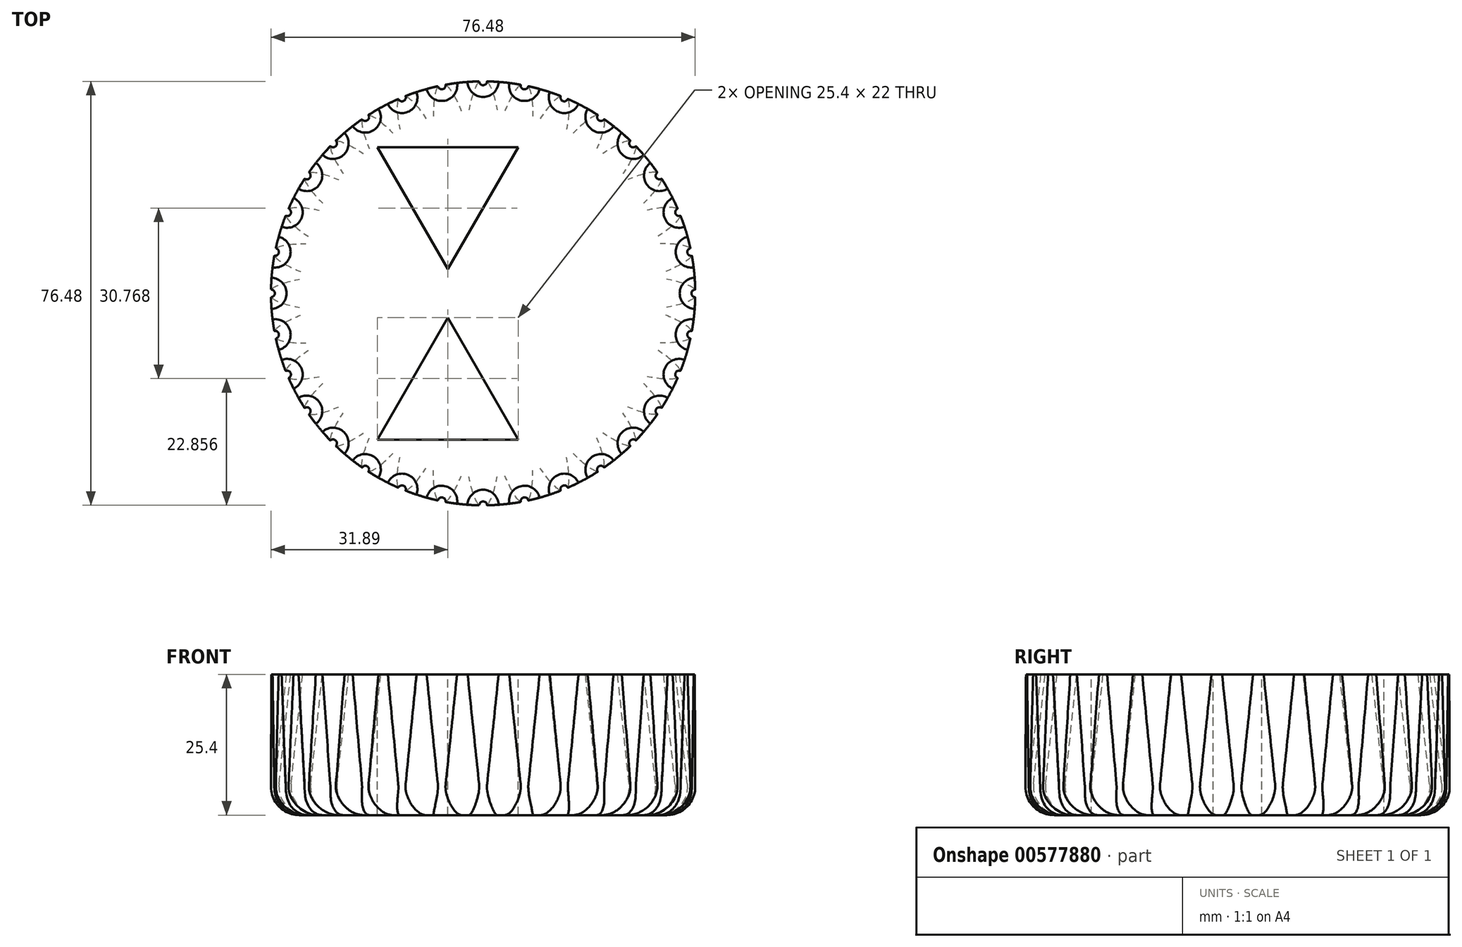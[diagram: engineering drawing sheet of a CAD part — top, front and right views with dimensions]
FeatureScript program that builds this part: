
annotation { "Feature Type Name" : "Feature", "Feature Type Description" : "" }
export const myFeature = defineFeature(function(context is Context, id is Id, definition is map)
    precondition{}
    {
        {
            var Q0;
            Q0=qCreatedBy(makeId("Top.planeOp"),FACE);
            var sketch = newSketch(context, id + "F0", { "sketchPlane" : qUnion([Q0])});
            skCircle(sketch, "E0", {"center": v(0, 0) * mm, "radius": 38.25 * mm});
            skSolve(sketch);
        }
        {
            var Q0;
            Q0=makeQuery(id+"F0.imprint","IMPRINT",FACE,{"disambiguationData":[TD([[makeQuery(id+"F0.imprint","IMPRINT",EDGE,{"derivedFrom":sQuery(id+"F0.wireOp",EDGE,"E0")}),1.0]])]});
            var Q1;
            Q1=sQuery(id+"F0.wireOp",EDGE,"E0");
            extrude(context, id + "F1", {"entities" : qUnion([Q0]), "surfaceEntities" : qUnion([Q1]), "depth" : 25.4 * mm, "offsetDistance" : 25.4 * mm});
        }
        {
            var Q0;
            Q0=makeQuery(id+"F1.opExtrude","CAP_FACE",FACE,{"disambiguationData":[OSD([sQuery(id+"F0.wireOp",EDGE,"E0")])],"isStart":false});
            var sketch = newSketch(context, id + "F2", { "sketchPlane" : qUnion([Q0])});
            skCircle(sketch, "E1", {"center": v(0, 38.25) * mm, "radius": 2.8 * mm});
            skCircle(sketch, "E2.1.0", {"center": v(-7.46, 37.51) * mm, "radius": 2.8 * mm});
            skCircle(sketch, "E2.2.0", {"center": v(-14.64, 35.33) * mm, "radius": 2.8 * mm});
            skCircle(sketch, "E2.3.0", {"center": v(-21.25, 31.8) * mm, "radius": 2.8 * mm});
            skCircle(sketch, "E2.4.0", {"center": v(-27.04, 27.04) * mm, "radius": 2.8 * mm});
            skCircle(sketch, "E2.5.0", {"center": v(-31.8, 21.25) * mm, "radius": 2.8 * mm});
            skCircle(sketch, "E2.6.0", {"center": v(-35.33, 14.64) * mm, "radius": 2.8 * mm});
            skCircle(sketch, "E2.7.0", {"center": v(-37.51, 7.46) * mm, "radius": 2.8 * mm});
            skCircle(sketch, "E2.8.0", {"center": v(-38.25, 0) * mm, "radius": 2.8 * mm});
            skCircle(sketch, "E2.9.0", {"center": v(-37.51, -7.46) * mm, "radius": 2.8 * mm});
            skCircle(sketch, "E2.10.0", {"center": v(-35.33, -14.64) * mm, "radius": 2.8 * mm});
            skCircle(sketch, "E2.11.0", {"center": v(-31.8, -21.25) * mm, "radius": 2.8 * mm});
            skCircle(sketch, "E2.12.0", {"center": v(-27.04, -27.04) * mm, "radius": 2.8 * mm});
            skCircle(sketch, "E2.13.0", {"center": v(-21.25, -31.8) * mm, "radius": 2.8 * mm});
            skCircle(sketch, "E2.14.0", {"center": v(-14.64, -35.33) * mm, "radius": 2.8 * mm});
            skCircle(sketch, "E2.15.0", {"center": v(-7.46, -37.51) * mm, "radius": 2.8 * mm});
            skCircle(sketch, "E2.16.0", {"center": v(0, -38.25) * mm, "radius": 2.8 * mm});
            skCircle(sketch, "E2.17.0", {"center": v(7.46, -37.51) * mm, "radius": 2.8 * mm});
            skCircle(sketch, "E2.18.0", {"center": v(14.64, -35.33) * mm, "radius": 2.8 * mm});
            skCircle(sketch, "E2.19.0", {"center": v(21.25, -31.8) * mm, "radius": 2.8 * mm});
            skCircle(sketch, "E2.20.0", {"center": v(27.04, -27.04) * mm, "radius": 2.8 * mm});
            skCircle(sketch, "E2.21.0", {"center": v(31.8, -21.25) * mm, "radius": 2.8 * mm});
            skCircle(sketch, "E2.22.0", {"center": v(35.33, -14.64) * mm, "radius": 2.8 * mm});
            skCircle(sketch, "E2.23.0", {"center": v(37.51, -7.46) * mm, "radius": 2.8 * mm});
            skCircle(sketch, "E2.24.0", {"center": v(38.25, 0) * mm, "radius": 2.8 * mm});
            skPoint(sketch, "E2.center", {"position": v(0, 0) * mm});
            skCircle(sketch, "E3.1.25.0", {"center": v(37.51, 7.46) * mm, "radius": 2.8 * mm});
            skCircle(sketch, "E4.1.26.0", {"center": v(35.33, 14.64) * mm, "radius": 2.8 * mm});
            skCircle(sketch, "E4.1.27.0", {"center": v(31.8, 21.25) * mm, "radius": 2.8 * mm});
            skCircle(sketch, "E4.1.28.0", {"center": v(27.04, 27.04) * mm, "radius": 2.8 * mm});
            skCircle(sketch, "E4.1.29.0", {"center": v(21.25, 31.8) * mm, "radius": 2.8 * mm});
            skCircle(sketch, "E4.1.30.0", {"center": v(14.64, 35.33) * mm, "radius": 2.8 * mm});
            skCircle(sketch, "E4.1.31.0", {"center": v(7.46, 37.51) * mm, "radius": 2.8 * mm});
            skSolve(sketch);
        }
        {
            var Q0;
            Q0 = qSketchRegion(id + "F2", true);
            extrude(context, id + "F3", {"entities" : qUnion([Q0]), "operationType" : NewBodyOperationType.REMOVE, "oppositeDirection" : true, "depth" : 25.4 * mm, "offsetDistance" : 25.4 * mm, "hasDraft" : true, "draftAngle" : 6 * degree, "draftPullDirection" : true});
        }
        {
            var Q0;
            {var subQ0=sQuery(id+"F0.wireOp",EDGE,"E0");Q0=makeQuery(id+"F3.boolean.opBoolean","SPLIT",EDGE,{"disambiguationData":[TD([makeQuery(id+"F1.opExtrude","SWEPT_FACE",FACE,{"disambiguationData":[OSD([subQ0])]}),makeQuery(id+"F1.opExtrude","CAP_FACE",FACE,{"disambiguationData":[OSD([subQ0])],"isStart":true}),makeQuery(id+"F3.opExtrude","SWEPT_FACE",FACE,{"disambiguationData":[OSD([sQuery(id+"F2.wireOp",EDGE,"E3.1.25.0")])]}),makeQuery(id+"F3.opExtrude","SWEPT_FACE",FACE,{"disambiguationData":[OSD([sQuery(id+"F2.wireOp",EDGE,"E4.1.26.0")])]})])],"derivedFrom":makeQuery(id+"F1.opExtrude","CAP_EDGE",EDGE,{"disambiguationData":[OSD([subQ0])],"isStart":true})});}
            var Q1;
            Q1=makeQuery(id+"F1.opExtrude","CAP_FACE",FACE,{"disambiguationData":[OSD([sQuery(id+"F0.wireOp",EDGE,"E0")])],"isStart":true});
            fillet(context, id + "F4", {"entities" : qUnion([Q0, Q1]), "radius" : 5.08 * mm, "tangentPropagation" : true, "allowEdgeOverflow" : false});
        }
        {
            var Q0;
            Q0=makeQuery(id+"F1.opExtrude","CAP_FACE",FACE,{"disambiguationData":[OSD([sQuery(id+"F0.wireOp",EDGE,"E0")])],"isStart":false});
            var sketch = newSketch(context, id + "F5", { "sketchPlane" : qUnion([Q0])});
            skLineSegment(sketch, "E5", {"start": v(-35.44, 0) * mm, "end": v(35.44, 0) * mm, "construction": true});
            skCircle(sketch, "E6.cCircle", {"center": v(-6.35, 19.05) * mm, "radius": 7.33 * mm, "construction": true});
            skLineSegment(sketch, "E6.0", {"start": v(6.35, 26.38) * mm, "end": v(-6.35, 4.39) * mm});
            skLineSegment(sketch, "E6.1", {"start": v(-6.35, 4.39) * mm, "end": v(-19.05, 26.38) * mm});
            skLineSegment(sketch, "E6.2", {"start": v(-19.05, 26.38) * mm, "end": v(6.35, 26.38) * mm});
            skPoint(sketch, "E6.0.midPoint", {"position": v(0, 15.38) * mm});
            skPoint(sketch, "E7.MirrorP", {"position": v(0, -15.38) * mm});
            skLineSegment(sketch, "E8.MirrorCS", {"start": v(-19.05, -26.38) * mm, "end": v(6.35, -26.38) * mm});
            skCircle(sketch, "E9.MirrorC", {"center": v(-6.35, -19.05) * mm, "radius": 7.33 * mm, "construction": true});
            skLineSegment(sketch, "E10.MirrorCS", {"start": v(6.35, -26.38) * mm, "end": v(-6.35, -4.39) * mm});
            skLineSegment(sketch, "E11.MirrorCS", {"start": v(-6.35, -4.39) * mm, "end": v(-19.05, -26.38) * mm});
            skSolve(sketch);
        }
        {
            var Q0;
            Q0 = qSketchRegion(id + "F5", true);
            extrude(context, id + "F6", {"entities" : qUnion([Q0]), "operationType" : NewBodyOperationType.REMOVE, "oppositeDirection" : true, "depth" : 25.4 * mm, "offsetDistance" : 25.4 * mm});
        }
    });
